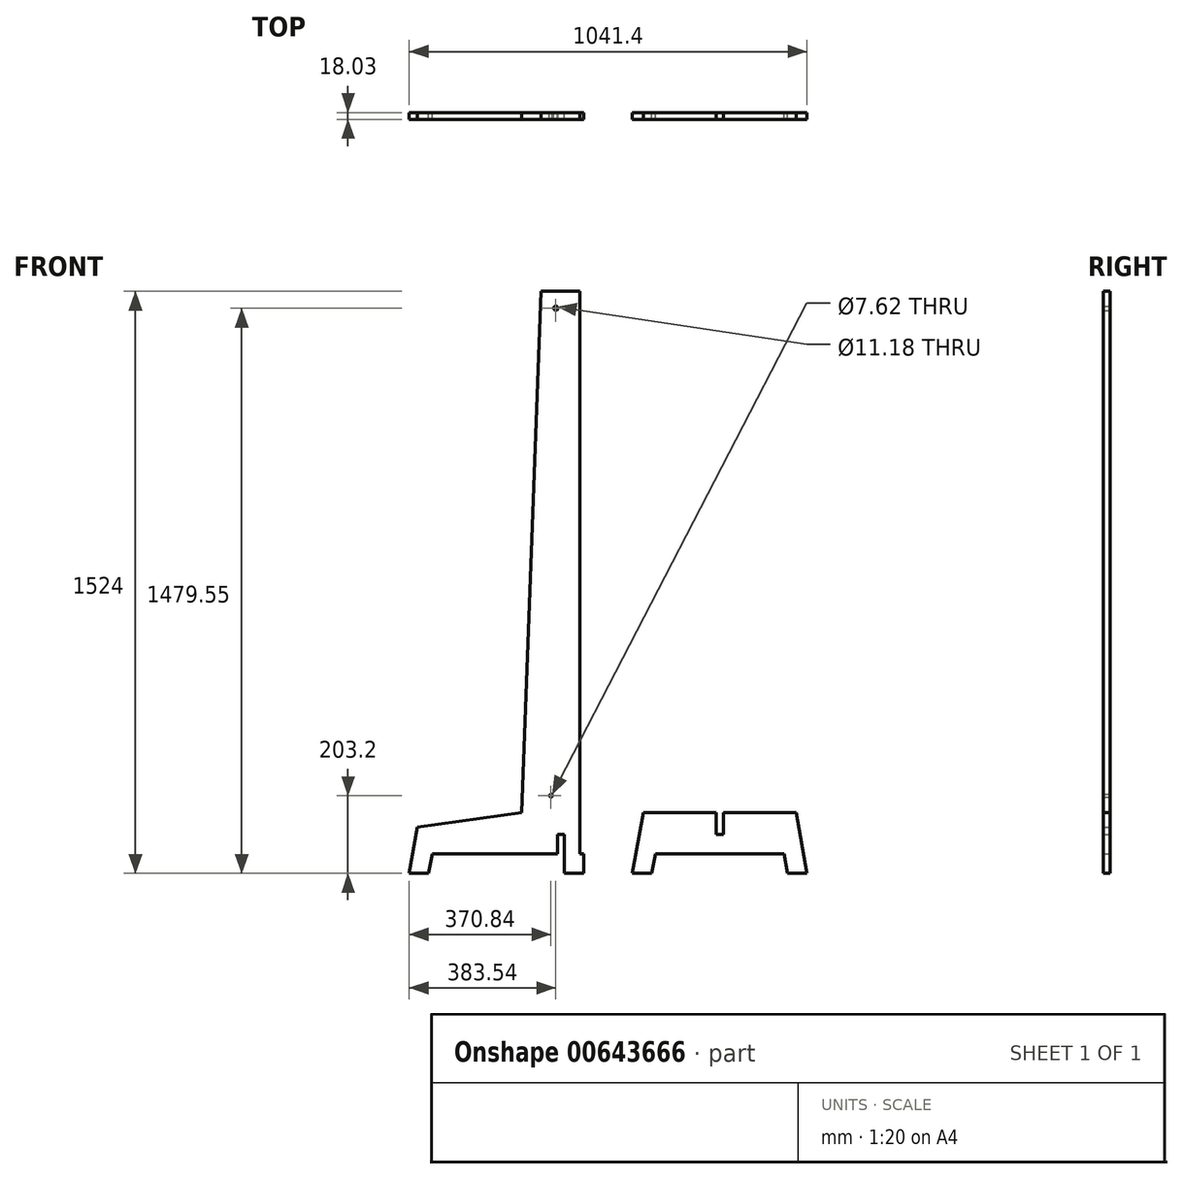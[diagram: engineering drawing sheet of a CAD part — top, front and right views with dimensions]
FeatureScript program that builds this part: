
annotation { "Feature Type Name" : "Feature", "Feature Type Description" : "" }
export const myFeature = defineFeature(function(context is Context, id is Id, definition is map)
    precondition{}
    {
        {
            var Q0;
            Q0=qCreatedBy(makeId("Front.planeOp"),FACE);
            var sketch = newSketch(context, id + "F0", { "sketchPlane" : qUnion([Q0])});
            skLineSegment(sketch, "E0", {"start": v(0, 0) * mm, "end": v(0, 1473.2) * mm});
            skLineSegment(sketch, "E1", {"start": v(0, 1473.2) * mm, "end": v(-101.6, 1473.2) * mm});
            skLineSegment(sketch, "E2", {"start": v(-101.6, 1473.2) * mm, "end": v(-152.4, 107.95) * mm});
            skLineSegment(sketch, "E3", {"start": v(0, 0) * mm, "end": v(10.16, 0) * mm});
            skLineSegment(sketch, "E4", {"start": v(10.16, 0) * mm, "end": v(10.16, -50.8) * mm});
            skLineSegment(sketch, "E5", {"start": v(10.16, -50.8) * mm, "end": v(-40.64, -50.8) * mm});
            skLineSegment(sketch, "E6", {"start": v(-40.64, -50.8) * mm, "end": v(-40.64, 50.8) * mm});
            skLineSegment(sketch, "E7", {"start": v(-40.64, 50.8) * mm, "end": v(-58.67, 50.8) * mm});
            skLineSegment(sketch, "E8", {"start": v(-58.67, 50.8) * mm, "end": v(-58.67, 0) * mm});
            skLineSegment(sketch, "E9", {"start": v(-58.67, 0) * mm, "end": v(-387.28, 0) * mm});
            skLineSegment(sketch, "E10", {"start": v(-387.28, 0) * mm, "end": v(-396.24, -50.8) * mm});
            skLineSegment(sketch, "E11", {"start": v(-396.24, -50.8) * mm, "end": v(-447.04, -50.8) * mm});
            skLineSegment(sketch, "E12", {"start": v(-447.04, -50.8) * mm, "end": v(-425.7, 70.18) * mm});
            skLineSegment(sketch, "E13", {"start": v(-425.7, 70.18) * mm, "end": v(-152.4, 107.95) * mm});
            skLineSegment(sketch, "E14", {"start": v(137.16, -50.8) * mm, "end": v(165.15, 107.95) * mm});
            skLineSegment(sketch, "E15", {"start": v(165.15, 107.95) * mm, "end": v(566.37, 107.95) * mm});
            skLineSegment(sketch, "E16", {"start": v(566.37, 107.95) * mm, "end": v(594.36, -50.8) * mm});
            skLineSegment(sketch, "E17", {"start": v(137.16, -50.8) * mm, "end": v(187.96, -50.8) * mm});
            skLineSegment(sketch, "E18", {"start": v(187.96, -50.8) * mm, "end": v(196.92, 0) * mm});
            skLineSegment(sketch, "E19", {"start": v(196.92, 0) * mm, "end": v(534.6, 0) * mm});
            skLineSegment(sketch, "E20", {"start": v(534.6, 0) * mm, "end": v(543.56, -50.8) * mm});
            skLineSegment(sketch, "E21", {"start": v(543.56, -50.8) * mm, "end": v(594.36, -50.8) * mm});
            skLineSegment(sketch, "E22.bottom", {"start": v(356.74, 50.8) * mm, "end": v(374.78, 50.8) * mm});
            skLineSegment(sketch, "E22.top", {"start": v(356.74, 107.95) * mm, "end": v(374.78, 107.95) * mm});
            skLineSegment(sketch, "E22.left", {"start": v(356.74, 50.8) * mm, "end": v(356.74, 107.95) * mm});
            skLineSegment(sketch, "E22.right", {"start": v(374.78, 50.8) * mm, "end": v(374.78, 107.95) * mm});
            skPoint(sketch, "E22.middle", {"position": v(365.76, 79.38) * mm});
            skPoint(sketch, "E22.middle.positionSnap0", {"position": v(365.76, 107.95) * mm});
            skPoint(sketch, "E22.centerSnap0", {"position": v(365.76, 107.95) * mm});
            skCircle(sketch, "E23", {"center": v(-76.2, 152.4) * mm, "radius": 3.81 * mm});
            skCircle(sketch, "E24", {"center": v(-63.5, 1428.75) * mm, "radius": 5.59 * mm});
            skSolve(sketch);
        }
        {
            var Q0;
            Q0=makeQuery(id+"F0.imprint","IMPRINT",FACE,{"disambiguationData":[TD([[makeQuery(id+"F0.imprint","IMPRINT",EDGE,{"derivedFrom":sQuery(id+"F0.wireOp",EDGE,"E0")}),1.0]])]});
            var Q1;
            {var subQ0=sQuery(id+"F0.wireOp",EDGE,"E14");Q1=makeQuery(id+"F0.imprint","IMPRINT",FACE,{"disambiguationData":[TD([[makeQuery(id+"F0.imprint","IMPRINT",EDGE,{"derivedFrom":subQ0}),-1.0]])]});}
            extrude(context, id + "F1", {"entities" : qUnion([Q0, Q1]), "depth" : 18.03 * mm, "offsetDistance" : 25.4 * mm});
        }
    });
